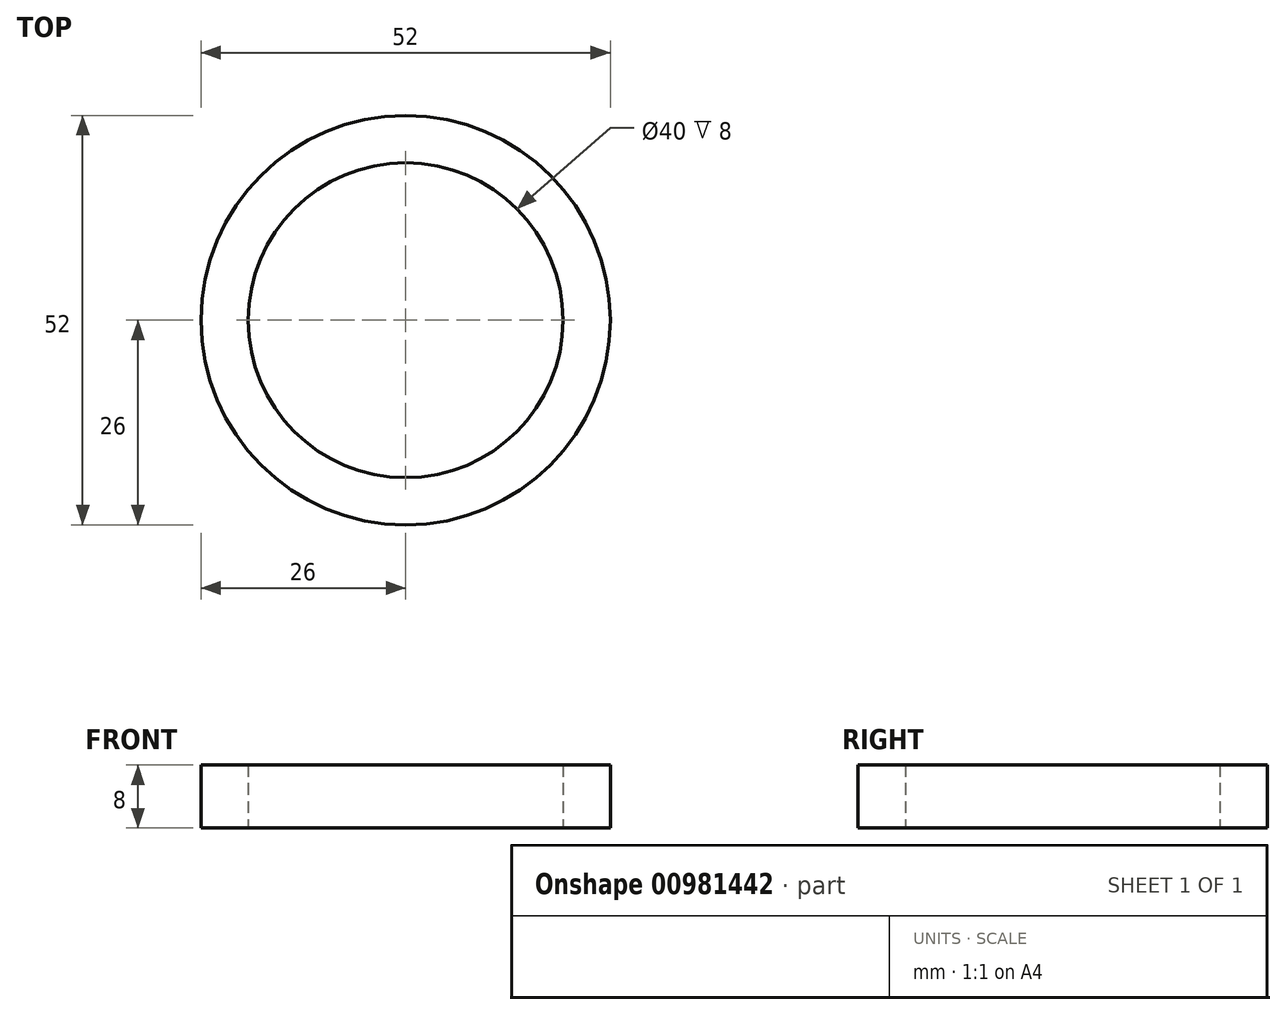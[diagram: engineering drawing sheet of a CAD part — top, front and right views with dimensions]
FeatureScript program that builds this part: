
annotation { "Feature Type Name" : "Feature", "Feature Type Description" : "" }
export const myFeature = defineFeature(function(context is Context, id is Id, definition is map)
    precondition{}
    {
        {
            var Q0;
            Q0=qCreatedBy(makeId("Top.planeOp"),FACE);
            var sketch = newSketch(context, id + "F0", { "sketchPlane" : qUnion([Q0])});
            skCircle(sketch, "E0", {"center": v(0, 0) * mm, "radius": 26 * mm});
            skCircle(sketch, "E1", {"center": v(0, 0) * mm, "radius": 20 * mm});
            skSolve(sketch);
        }
        {
            var Q0;
            Q0=makeQuery(id+"F0.imprint","IMPRINT",FACE,{"disambiguationData":[TD([[makeQuery(id+"F0.imprint","IMPRINT",EDGE,{"derivedFrom":sQuery(id+"F0.wireOp",EDGE,"E0")}),1.0]])]});
            extrude(context, id + "F1", {"entities" : qUnion([Q0]), "depth" : 8 * mm, "offsetDistance" : 25 * mm});
        }
    });
